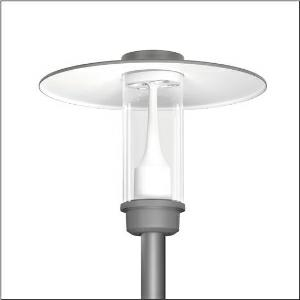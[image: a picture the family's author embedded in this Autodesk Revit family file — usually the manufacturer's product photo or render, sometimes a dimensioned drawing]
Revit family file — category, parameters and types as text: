
# Revit family: litepole_2_iq___pl1_2s_5xa5425jf14h000022_13c4
name_source: partatom
category: Lighting Fixtures
units: mm (PartAtom-declared; Revit-internal decimal feet)

## family parameters
Cut with Voids When Loaded = No
Host = Face
Light Source = No
Part Type = Normal
Room Calculation Point = No
Round Connector Dimension = Use Diameter
Shared = No

## types (1)
- --- (1 x LED, 2990 lm, 19.3 W, 3000K)
    Apparent Load = 19 VA
    CIE Flux Codes = 22 60 92 98 100
    Color Rendering = 70
    Color Temperature = 3000K
    Default Elevation = 1800 mm
    Description = Litepole 2 iQ, mast luminaire, Module 540 iQ-SR, primary light control with 3 zone facetted reflector, of plastic, silver coated, highly specular, structured, primary optical cover: cover, of PMMA, transparent, light distribution: PL1.2s, light emission: direct distribution, primary light characteristic: symmetric, installation type: post-top, LED, High Power LED, rated luminous flux: 2.990lm, luminous efficacy: 155lm/W, light colour: 730, colour temperature: 3000K, control gear: iQ Street-Remote, control: Street-Remote, Auto-Match, Temp-Guard, Lumen-Switch, Night-Set, Smart-Wire, Light-Fading, Desk-Remote (wireless, voltage-free reading and setting of iQ features in the workshop via application-optimized NFC function/RFID function), optimised constant luminous flux control (CLO 2.0), pre-setting: logarithmic dimming characteristic, mains connection: 230..240V, AC, 50/60Hz, connection cable pre-assembled, cable length: 5,5m, wiring characteristics: H07RN-F, start of lifetime: 19W, end of service life: 21W, reduction: 10W, luminaire housing, upper part, of aluminium, coated, Siteco® metallic grey (DB 702S), diameter: 750mm, height: 590mm, spigot size: d x l = 76 x 70mm (post-top) | with reducer (optional accessory) 60 x 70mm, mounting height: 3..5m, post-top mast mounting element, of diecast aluminium, coated, Siteco® metallic grey (DB 702S), Module 540 iQ-SR, traffic white (RAL 9016), equipment: standard, protection rating (complete): IP65, insulation class (complete): insulation class II (safety insulation), certification: CE, ENEC, VDE, packaging unit: 1 piece

Light Distribution: PL1.2s
    Height = 590 mm
    Lamp = 1 x LED
    Lamp Light Flux = 2990 lm
    Lamp Power = 19.3 W
    Lamp count = 1
    Length = 750 mm
    Luminous efficacy = 155 lm/W
    Manufacturer = Siteco
    ModVariant = No
    Model = 5XA5425JF14H000022
    Number of Poles = 1
    OnlyDefault = Yes
    Power Factor = 1
    Product Name = Litepole 2 iQ | PL1.2s
    Product group = mast luminaire | pylon top
    ProductGroupID = 6100
    Protection Class = Protection class II
    Protection Degree = IP 65
    RLX_Detail_Level = 1
    RLX_Emergency_Light_Flux = 0 lm
    RLX_Emergency_Type = 0
    RLX_Emergency_Type_DB = No
    RlxData = <blob elided: 29441 chars, md5=07b224c7>
    Socket = socket
    Standby Power = 0 W
    System Light Flux = 2990 lm
    System Power = 19 W
    Type Comments = factory setting: luminous flux: 100 % | dim-lin: 254 | 403 mA
    Type Image = l_1006518.jpg
    URL = http://relux.com
    VarID = @adj_144574
    Voltage = 0 V
    Weight = 0.00 kg
    Width = 0 mm  [stored 0 ft]

note: [stored X ft] marks values corroborated as IEEE doubles in the binary element streams (Revit-internal decimal feet)

## geometry (parser evidence)
native form markers: Blend x4, Sweep x11
no freeform markers — native parametric forms only
